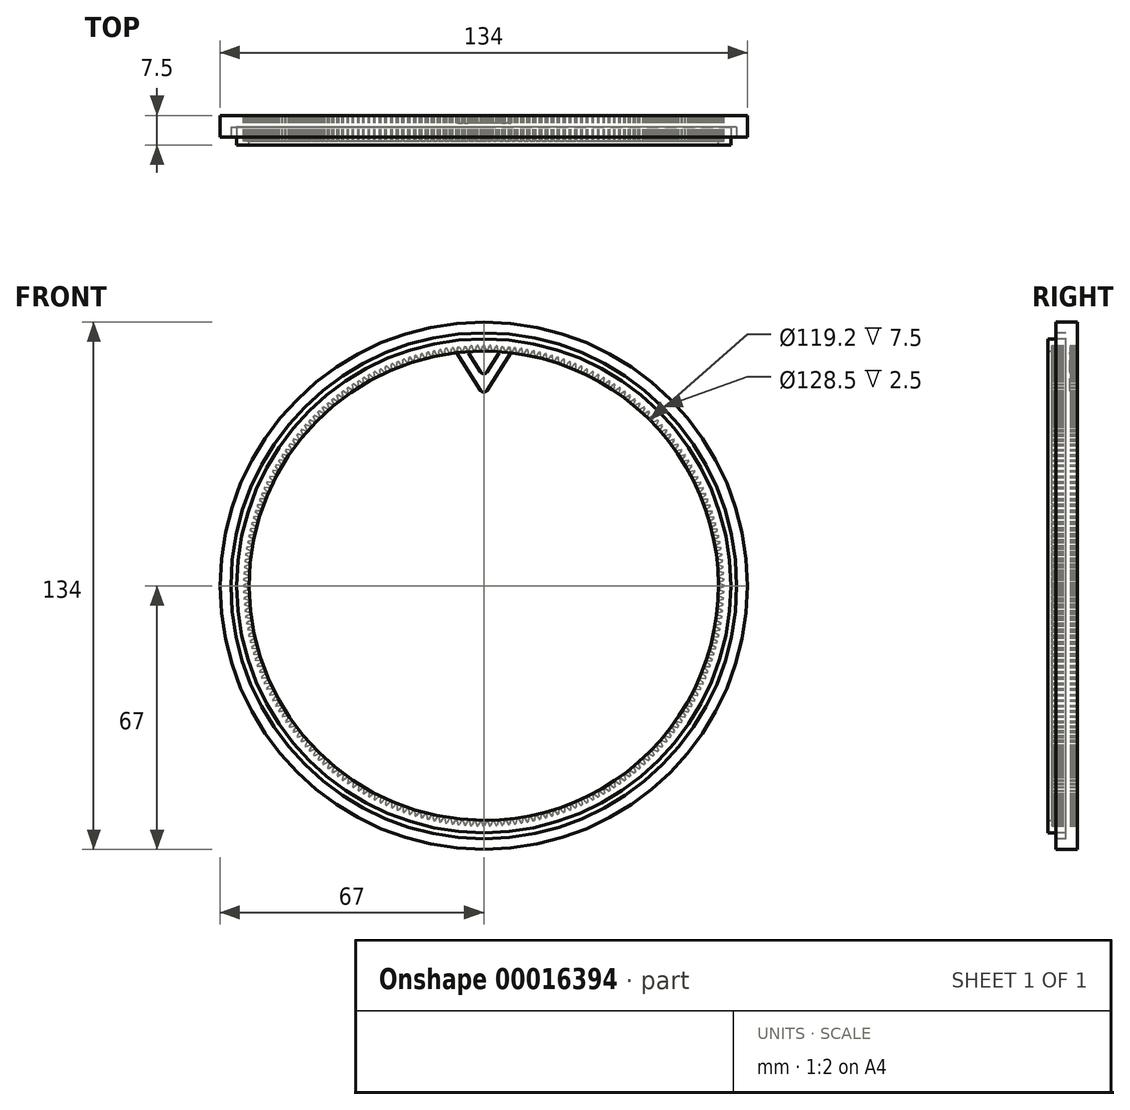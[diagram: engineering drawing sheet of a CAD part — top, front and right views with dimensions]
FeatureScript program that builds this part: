
annotation { "Feature Type Name" : "Feature", "Feature Type Description" : "" }
export const myFeature = defineFeature(function(context is Context, id is Id, definition is map)
    precondition{}
    {
        {
            var Q0;
            Q0=qCreatedBy(makeId("Front.planeOp"),FACE);
            var sketch = newSketch(context, id + "F0", { "sketchPlane" : qUnion([Q0])});
            skCircle(sketch, "E0", {"center": v(0, 0) * mm, "radius": 67 * mm});
            skCircle(sketch, "E1", {"center": v(0, 0) * mm, "radius": 59.6 * mm});
            skSolve(sketch);
        }
        {
            var Q0;
            Q0=makeQuery(id+"F0.imprint","IMPRINT",FACE,{"disambiguationData":[TD([[makeQuery(id+"F0.imprint","IMPRINT",EDGE,{"derivedFrom":sQuery(id+"F0.wireOp",EDGE,"E0")}),1.0]])]});
            extrude(context, id + "F1", {"entities" : qUnion([Q0]), "depth" : 7.5 * mm});
        }
        {
            var Q0;
            Q0=makeQuery(id+"F1.opExtrude","CAP_FACE",FACE,{"disambiguationData":[OSD([sQuery(id+"F0.wireOp",EDGE,"E0"),sQuery(id+"F0.wireOp",EDGE,"E1")])],"isStart":false});
            var sketch = newSketch(context, id + "F2", { "sketchPlane" : qUnion([Q0])});
            skCircle(sketch, "E2", {"center": v(0, 0) * mm, "radius": 63.5 * mm, "construction": true});
            skCircle(sketch, "E3", {"center": v(0, 0) * mm, "radius": 64.25 * mm});
            skCircle(sketch, "E4", {"center": v(0, 0) * mm, "radius": 62.75 * mm});
            skLineSegment(sketch, "E5", {"start": v(0, 62.75) * mm, "end": v(0, 63.5) * mm, "construction": true});
            skLineSegment(sketch, "E6", {"start": v(0, 64.25) * mm, "end": v(0, 63.5) * mm, "construction": true});
            skSolve(sketch);
        }
        {
            var Q0;
            Q0 = qSketchRegion(id + "F2", true);
            extrude(context, id + "F3", {"entities" : qUnion([Q0]), "operationType" : NewBodyOperationType.REMOVE, "oppositeDirection" : true, "depth" : 4.5 * mm});
        }
        {
            var Q0;
            Q0=makeQuery(id+"F2.imprint","IMPRINT",FACE,{"disambiguationData":[TD([[makeQuery(id+"F2.imprint","IMPRINT",EDGE,{"derivedFrom":sQuery(id+"F2.wireOp",EDGE,"E3")}),-1.0]])]});
            extrude(context, id + "F4", {"entities" : qUnion([Q0]), "operationType" : NewBodyOperationType.REMOVE, "oppositeDirection" : true, "depth" : 2 * mm});
        }
        {
            var Q0;
            Q0=makeQuery(id+"F1.opExtrude","CAP_FACE",FACE,{"disambiguationData":[OSD([sQuery(id+"F0.wireOp",EDGE,"E0"),sQuery(id+"F0.wireOp",EDGE,"E1")])],"isStart":true});
            var sketch = newSketch(context, id + "F5", { "sketchPlane" : qUnion([Q0])});
            skCircle(sketch, "E7", {"center": v(0, 0) * mm, "radius": 61 * mm, "construction": true});
            skLineSegment(sketch, "E8", {"start": v(59.6, 0.67) * mm, "end": v(59.6, -0.67) * mm});
            skLineSegment(sketch, "E9", {"start": v(0, 0) * mm, "end": v(59.6, 0) * mm, "construction": true});
            skLineSegment(sketch, "E10", {"start": v(61, 0.15) * mm, "end": v(61, -0.15) * mm});
            skLineSegment(sketch, "E11", {"start": v(59.6, 0) * mm, "end": v(61, 0) * mm, "construction": true});
            skLineSegment(sketch, "E12", {"start": v(59.6, 0.68) * mm, "end": v(61, 0.15) * mm});
            skLineSegment(sketch, "E13", {"start": v(59.6, -0.68) * mm, "end": v(61, -0.15) * mm});
            skSolve(sketch);
        }
        {
            var Q0;
            Q0 = qSketchRegion(id + "F5", true);
            extrude(context, id + "F6", {"entities" : qUnion([Q0]), "operationType" : NewBodyOperationType.REMOVE, "oppositeDirection" : true, "depth" : 6.5 * mm});
        }
        {
            var Q0;
            Q0=makeQuery(id+"F6.boolean.opBoolean","COPY",FACE,{"derivedFrom":makeQuery(id+"F6.opExtrude","CAP_FACE",FACE,{"disambiguationData":[OSD([sQuery(id+"F5.wireOp",EDGE,"E8"),sQuery(id+"F5.wireOp",EDGE,"E10"),sQuery(id+"F5.wireOp",EDGE,"E12"),sQuery(id+"F5.wireOp",EDGE,"E13")])],"isStart":false})});
            var Q1;
            Q1=makeQuery(id+"F6.boolean.opBoolean","COPY",FACE,{"derivedFrom":makeQuery(id+"F6.opExtrude","SWEPT_FACE",FACE,{"disambiguationData":[OSD([sQuery(id+"F5.wireOp",EDGE,"E12")])]})});
            var Q2;
            Q2=makeQuery(id+"F6.boolean.opBoolean","COPY",FACE,{"derivedFrom":makeQuery(id+"F6.opExtrude","SWEPT_FACE",FACE,{"disambiguationData":[OSD([sQuery(id+"F5.wireOp",EDGE,"E10")])]})});
            var Q3;
            Q3=makeQuery(id+"F6.boolean.opBoolean","COPY",FACE,{"derivedFrom":makeQuery(id+"F6.opExtrude","SWEPT_FACE",FACE,{"disambiguationData":[OSD([sQuery(id+"F5.wireOp",EDGE,"E13")])]})});
            var Q4;
            Q4=makeQuery(id+"F1.opExtrude","SWEPT_FACE",FACE,{"disambiguationData":[OSD([sQuery(id+"F0.wireOp",EDGE,"E1")])]});
            circularPattern(context, id + "F7", {"faces" : qUnion([Q0, Q1, Q2, Q3]), "axis" : qUnion([Q4]), "angle" : 360 * degree, "instanceCount" : 240, "equalSpace" : true, "patternType" : PatternType.FACE});
        }
        {
            var Q0;
            Q0=makeQuery(id+"F1.opExtrude","CAP_FACE",FACE,{"disambiguationData":[OSD([sQuery(id+"F0.wireOp",EDGE,"E0"),sQuery(id+"F0.wireOp",EDGE,"E1")])],"isStart":true});
            var sketch = newSketch(context, id + "F8", { "sketchPlane" : qUnion([Q0])});
            skLineSegment(sketch, "E14", {"start": v(-8.73, 62.1) * mm, "end": v(8.73, 62.1) * mm});
            skLineSegment(sketch, "E15", {"start": v(-8.73, 62.1) * mm, "end": v(0, 48.33) * mm});
            skLineSegment(sketch, "E16", {"start": v(0, 48.33) * mm, "end": v(8.73, 62.1) * mm});
            skLineSegment(sketch, "E17", {"start": v(0, 0) * mm, "end": v(0, 48.33) * mm, "construction": true});
            skLineSegment(sketch, "E18", {"start": v(0, 0) * mm, "end": v(8.73, 62.1) * mm, "construction": true});
            skLineSegment(sketch, "E19", {"start": v(0, 0) * mm, "end": v(-8.73, 62.1) * mm, "construction": true});
            skLineSegment(sketch, "E20.0", {"start": v(-4.18, 59.6) * mm, "end": v(0, 53) * mm});
            skLineSegment(sketch, "E20.1", {"start": v(-4.18, 59.6) * mm, "end": v(4.18, 59.6) * mm});
            skLineSegment(sketch, "E20.2", {"start": v(0, 53) * mm, "end": v(4.18, 59.6) * mm});
            skSolve(sketch);
        }
        {
            var Q0;
            {var subQ3=sQuery(id+"F8.wireOp",EDGE,"E16");var subQ7=sQuery(id+"F8.wireOp",EDGE,"E15");var subQ10=makeQuery(id+"F8.imprint","INTERSECT",VERTEX,{"derivedFrom":[subQ7,subQ3]});Q0=makeQuery(id+"F8.imprint","IMPRINT",FACE,{"disambiguationData":[TD([[makeQuery(id+"F8.imprint","IMPRINT",EDGE,{"disambiguationData":[TD([[subQ10,1.0]])],"derivedFrom":subQ7}),1.0]])]});}
            var Q1;
            {var subQ13=sQuery(id+"F8.wireOp",EDGE,"E14");Q1=makeQuery(id+"F8.imprint","IMPRINT",FACE,{"disambiguationData":[TD([[makeQuery(id+"F8.imprint","IMPRINT",EDGE,{"derivedFrom":subQ13}),-1.0]])]});}
            extrude(context, id + "F9", {"entities" : qUnion([Q0, Q1]), "operationType" : NewBodyOperationType.ADD, "oppositeDirection" : true, "depth" : 2 * mm});
        }
        {
            var Q0;
            Q0=makeQuery(id+"F9.opExtrude","SWEPT_EDGE",EDGE,{"disambiguationData":[OSD([sQuery(id+"F8.wireOp",EDGE,"E15"),sQuery(id+"F8.wireOp",EDGE,"E16")])]});
            var Q1;
            Q1=makeQuery(id+"F9.opExtrude","SWEPT_EDGE",EDGE,{"disambiguationData":[OSD([sQuery(id+"F8.wireOp",EDGE,"E20.1"),sQuery(id+"F8.wireOp",EDGE,"E20.2")])]});
            var Q2;
            Q2=makeQuery(id+"F9.opExtrude","SWEPT_EDGE",EDGE,{"disambiguationData":[OSD([sQuery(id+"F8.wireOp",EDGE,"E20.0"),sQuery(id+"F8.wireOp",EDGE,"E20.2")])]});
            var Q3;
            Q3=makeQuery(id+"F9.opExtrude","SWEPT_EDGE",EDGE,{"disambiguationData":[OSD([sQuery(id+"F8.wireOp",EDGE,"E20.0"),sQuery(id+"F8.wireOp",EDGE,"E20.1")])]});
            fillet(context, id + "F10", {"entities" : qUnion([Q0, Q1, Q2, Q3]), "radius" : 1 * mm, "tangentPropagation" : true, "allowEdgeOverflow" : false});
        }
    });
